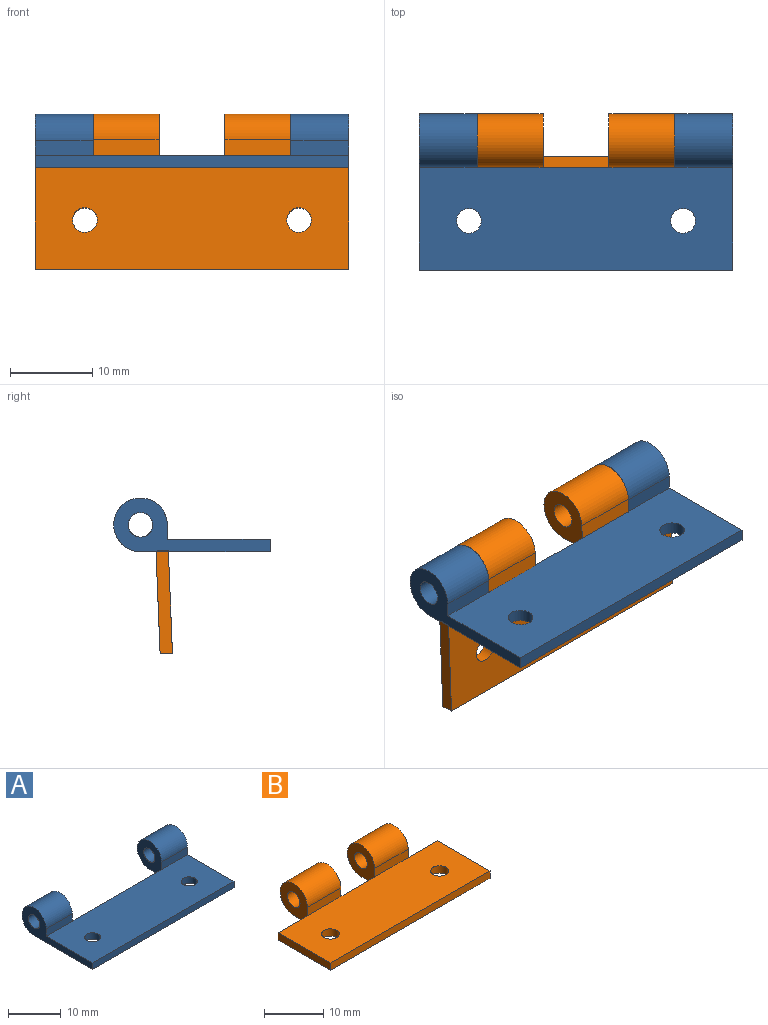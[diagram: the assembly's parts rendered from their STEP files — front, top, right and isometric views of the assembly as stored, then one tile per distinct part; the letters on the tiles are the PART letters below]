
ASSEMBLY  parts=2 mates=1
PART A: 16 faces, bbox 38x19x6.5 mm
  f0: plane 7x1.75mm, normal (0,-1,0), area 12.2mm2, adj f4,f7,f9,f13
  f1: plane 38x15.75mm, normal (0,0,-1), area 506.4mm2, adj f2,f4,f5,f6,f9,f11,f12,f13
  f2: cylinder r=3.25mm len=7mm, axis (-1,0,0), area 107.2mm2, adj f1,f5,f8,f12
  f3: cylinder r=1.5mm len=7mm, axis (-1,0,0), area 66mm2, adj f5,f12
  f4: plane 19x6.5mm, normal (1,0,0), area 47.1mm2, adj f0,f1,f6,f7,f9,f10
  f5: plane 19x6.5mm, normal (-1,0,0), area 47.1mm2, adj f1,f2,f3,f6,f7,f8
  f6: plane 38x1.5mm, normal (0,-1,0), area 57mm2, adj f1,f4,f5,f7
  f7: plane 38x12.5mm, normal (0,0,1), area 460.9mm2, adj f0,f4,f5,f6,f8,f11,f14,f15
  f8: plane 7x1.75mm, normal (0,-1,0), area 12.2mm2, adj f2,f5,f7,f12
  f9: cylinder r=3.25mm len=7mm, axis (-1,0,0), area 107.2mm2, adj f0,f1,f4,f13
  f10: cylinder r=1.5mm len=7mm, axis (-1,0,0), area 66mm2, adj f4,f13
  f11: plane 24x1.5mm, normal (0,1,0), area 36mm2, adj f1,f7,f12,f13
  f12: plane 6.5x6.5mm, normal (1,0,0), area 28.4mm2, adj f1,f2,f3,f8,f11
  f13: plane 6.5x6.5mm, normal (-1,0,0), area 28.4mm2, adj f0,f1,f9,f10,f11
  f14: cylinder r=1.5mm len=3mm, axis (0,0,1), area 14.1mm2, adj f1,f7
  f15: cylinder r=1.5mm len=3mm, axis (0,0,1), area 14.1mm2, adj f1,f7
PART B: 20 faces, bbox 38x19x6.5 mm
  f0: plane 38x15.75mm, normal (0,0,-1), area 512.9mm2, adj f4,f5,f6,f7,f8,f9,f10,f11
  f1: plane 38x12.5mm, normal (0,0,1), area 460.9mm2, adj f2,f3,f4,f5,f8,f9,f13,f15
  f2: plane 8x1.75mm, normal (0,-1,0), area 14mm2, adj f1,f6,f11,f16
  f3: plane 8x1.75mm, normal (0,-1,0), area 14mm2, adj f1,f7,f10,f14
  f4: plane 12.5x1.5mm, normal (1,0,0), area 18.8mm2, adj f0,f1,f8,f13
  f5: plane 12.5x1.5mm, normal (-1,0,0), area 18.8mm2, adj f0,f1,f8,f15
  f6: cylinder r=3.25mm len=8mm, axis (-1,0,0), area 122.5mm2, adj f0,f2,f11,f16
  f7: cylinder r=3.25mm len=8mm, axis (-1,0,0), area 122.5mm2, adj f0,f3,f10,f14
  f8: plane 38x1.5mm, normal (0,-1,0), area 57mm2, adj f0,f1,f4,f5
  f9: plane 8x1.5mm, normal (0,1,0), area 12mm2, adj f0,f1,f10,f11
  f10: plane 6.5x6.5mm, normal (-1,0,0), area 28.4mm2, adj f0,f3,f7,f9,f12
  f11: plane 6.5x6.5mm, normal (1,0,0), area 28.4mm2, adj f0,f2,f6,f9,f17
  f12: cylinder r=1.5mm len=8mm, axis (-1,0,0), area 75.4mm2, adj f10,f14
  f13: plane 7x1.5mm, normal (0,1,0), area 10.5mm2, adj f0,f1,f4,f14
  f14: plane 6.5x6.5mm, normal (1,0,0), area 28.4mm2, adj f0,f3,f7,f12,f13
  f15: plane 7x1.5mm, normal (0,1,0), area 10.5mm2, adj f0,f1,f5,f16
  f16: plane 6.5x6.5mm, normal (-1,0,0), area 28.4mm2, adj f0,f2,f6,f15,f17
  f17: cylinder r=1.5mm len=8mm, axis (-1,0,0), area 75.4mm2, adj f11,f16
  f18: cylinder r=1.5mm len=3mm, axis (0,0,1), area 14.1mm2, adj f0,f1
  f19: cylinder r=1.5mm len=3mm, axis (0,0,1), area 14.1mm2, adj f0,f1
PLACE A at identity fixed
PLACE B rot(axis=(0,0.72,0.69),180deg) t=(0,2.75,-2.87)mm
MATE revolute A.f2 <-> B.f6  axis (-1,0,0) through (12,6.25,3.25)mm
